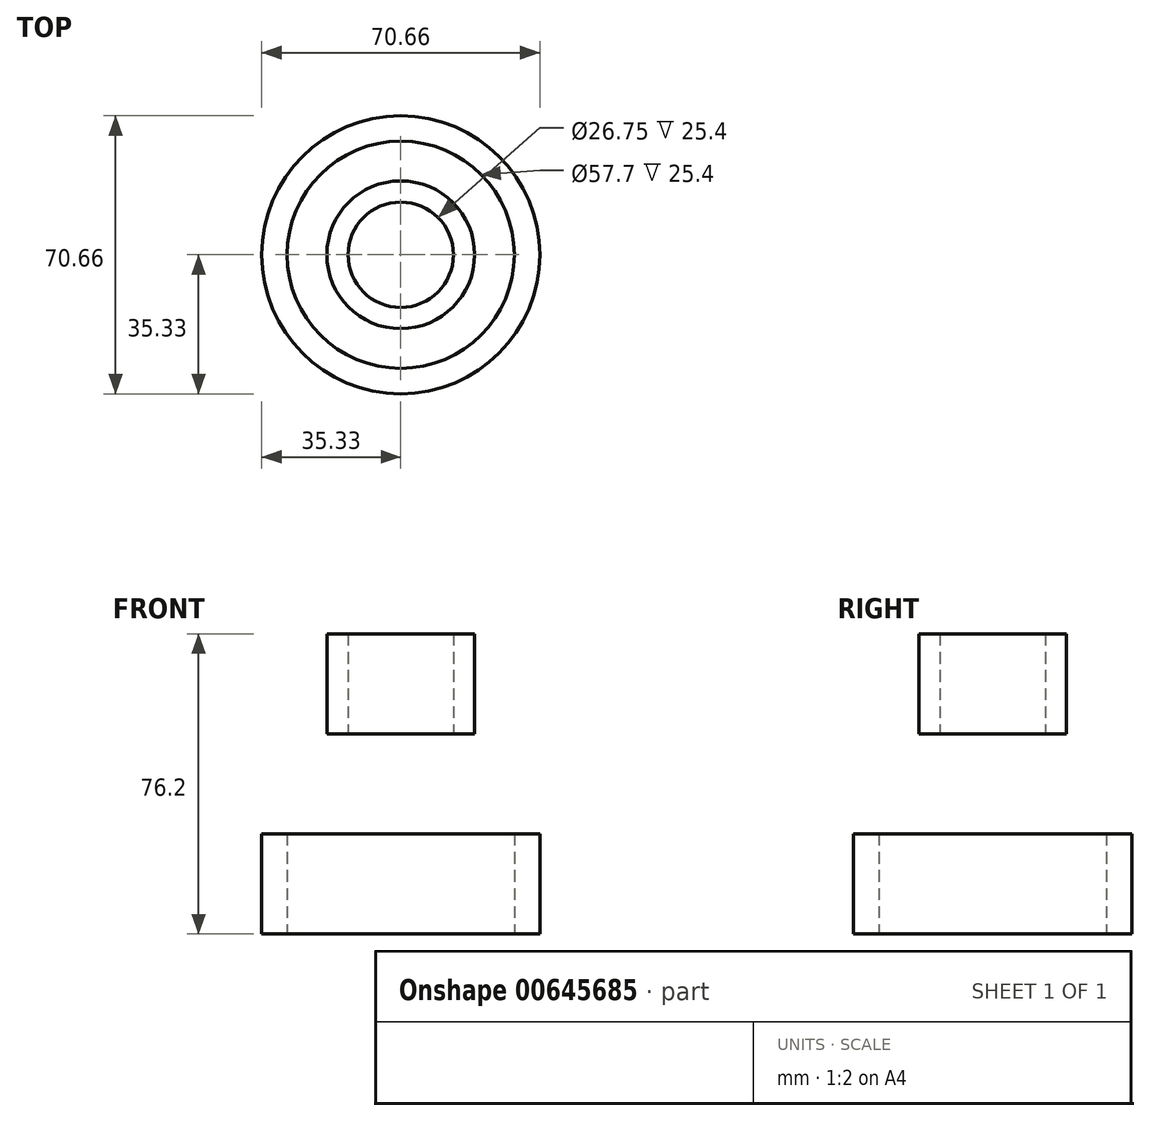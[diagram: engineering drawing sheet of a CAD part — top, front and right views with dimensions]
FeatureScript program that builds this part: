
annotation { "Feature Type Name" : "Feature", "Feature Type Description" : "" }
export const myFeature = defineFeature(function(context is Context, id is Id, definition is map)
    precondition{}
    {
        {
            var Q0;
            Q0=qCreatedBy(makeId("Top.planeOp"),FACE);
            var sketch = newSketch(context, id + "F0", { "sketchPlane" : qUnion([Q0])});
            skCircle(sketch, "E0", {"center": v(0, 0) * mm, "radius": 35.33 * mm});
            skCircle(sketch, "E1", {"center": v(0, 0) * mm, "radius": 28.85 * mm});
            skSolve(sketch);
        }
        {
            var Q0;
            Q0=makeQuery(id+"F0.imprint","IMPRINT",FACE,{"disambiguationData":[TD([[makeQuery(id+"F0.imprint","IMPRINT",EDGE,{"derivedFrom":sQuery(id+"F0.wireOp",EDGE,"E0")}),1.0]])]});
            extrude(context, id + "F1", {"entities" : qUnion([Q0]), "depth" : 25.4 * mm, "offsetDistance" : 25.4 * mm});
        }
        {
            var Q0;
            Q0=qCreatedBy(makeId("Top.planeOp"),FACE);
            cPlane(context, id + "F2", {"entities" : qUnion([Q0]), "cplaneType" : CPlaneType.OFFSET, "offset" : 50.8 * mm, "width" : 152.4 * mm, "height" : 152.4 * mm});
        }
        {
            var Q0;
            Q0=qCreatedBy(id+"F2.planeOp",FACE);
            var sketch = newSketch(context, id + "F3", { "sketchPlane" : qUnion([Q0])});
            skCircle(sketch, "E2", {"center": v(0, 0) * mm, "radius": 18.78 * mm});
            skCircle(sketch, "E3", {"center": v(0, 0) * mm, "radius": 13.38 * mm});
            skSolve(sketch);
        }
        {
            var Q0;
            Q0=makeQuery(id+"F3.imprint","IMPRINT",FACE,{"disambiguationData":[TD([[makeQuery(id+"F3.imprint","IMPRINT",EDGE,{"derivedFrom":sQuery(id+"F3.wireOp",EDGE,"E2")}),1.0]])]});
            extrude(context, id + "F4", {"entities" : qUnion([Q0]), "depth" : 25.4 * mm, "offsetDistance" : 25.4 * mm});
        }
        {
            var Q0;
            Q0=makeQuery(id+"F1.opExtrude","CAP_EDGE",EDGE,{"disambiguationData":[OSD([sQuery(id+"F0.wireOp",EDGE,"E1")])],"isStart":false});
            var Q1;
            Q1=makeQuery(id+"F4.opExtrude","CAP_EDGE",EDGE,{"disambiguationData":[OSD([sQuery(id+"F3.wireOp",EDGE,"E3")])],"isStart":true});
            loft(context, id + "F5", {"bodyType" : ToolBodyType.SURFACE, "wireProfilesArray" : [{ "wireProfileEntities" : qUnion([Q0]) }, { "wireProfileEntities" : qUnion([Q1]) }]});
        }
        {
            var Q0;
            Q0=makeQuery(id+"F1.opExtrude","CAP_EDGE",EDGE,{"disambiguationData":[OSD([sQuery(id+"F0.wireOp",EDGE,"E0")])],"isStart":false});
            var Q1;
            Q1=makeQuery(id+"F4.opExtrude","CAP_EDGE",EDGE,{"disambiguationData":[OSD([sQuery(id+"F3.wireOp",EDGE,"E2")])],"isStart":true});
            loft(context, id + "F6", {"bodyType" : ToolBodyType.SURFACE, "wireProfilesArray" : [{ "wireProfileEntities" : qUnion([Q0]) }, { "wireProfileEntities" : qUnion([Q1]) }]});
        }
    });
